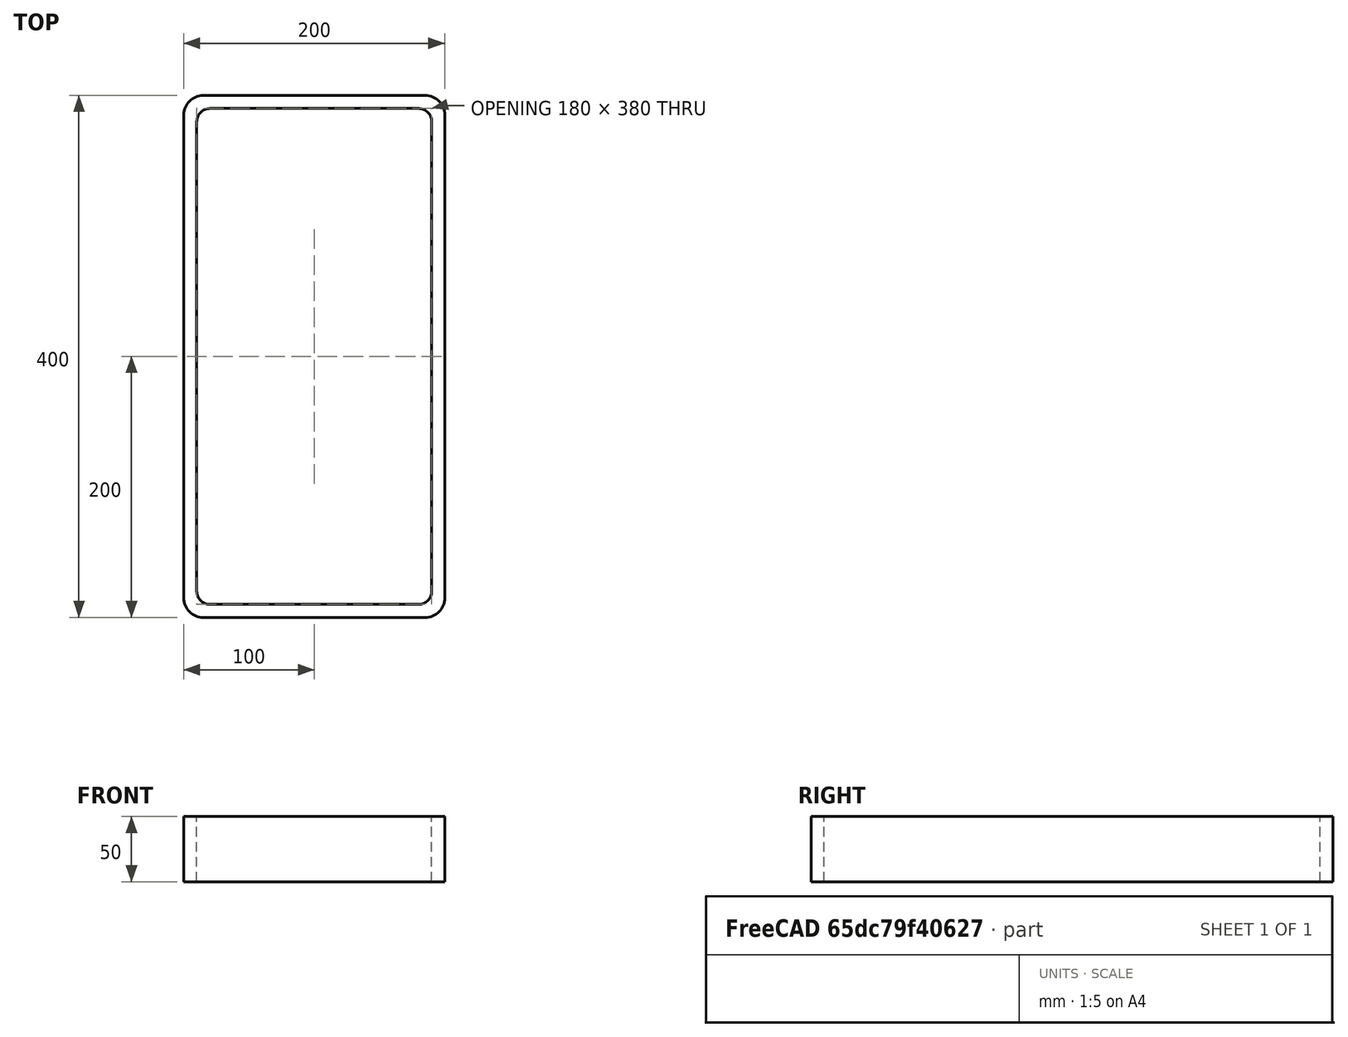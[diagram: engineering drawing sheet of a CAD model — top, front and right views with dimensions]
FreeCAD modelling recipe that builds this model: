
FCSTD DOCUMENT  (FreeCAD 0.15R4671 (Git))
Label: Rectangular hollow section 400x200x10 EN10219 S235JRH
License: All rights reserved
LicenseURL: http://en.wikipedia.org/wiki/All_rights_reserved
objects: Sketcher::SketchObject×1, Part::Extrusion×1
note: 2 computed .brp shape members not serialized (recipe doc carries the construction recipe); baked Part::Feature solids carry a one-line shape summary decoded from their .brp

FEATURE [Sketcher::SketchObject] Sketch
  sketch-geometry (16):
    g0: LineSegment StartX=-80 StartY=190 StartZ=0 EndX=80 EndY=190 EndZ=0
    g1: LineSegment StartX=90 StartY=180 StartZ=0 EndX=90 EndY=-180 EndZ=0
    g2: LineSegment StartX=80 StartY=-190 StartZ=0 EndX=-80 EndY=-190 EndZ=0
    g3: LineSegment StartX=-90 StartY=-180 StartZ=0 EndX=-90 EndY=180 EndZ=0
    g4: LineSegment StartX=-85 StartY=200 StartZ=0 EndX=85 EndY=200 EndZ=0
    g5: LineSegment StartX=100 StartY=185 StartZ=0 EndX=100 EndY=-185 EndZ=0
    g6: LineSegment StartX=85 StartY=-200 StartZ=0 EndX=-85 EndY=-200 EndZ=0
    g7: LineSegment StartX=-100 StartY=-185 StartZ=0 EndX=-100 EndY=185 EndZ=0
    g8: ArcOfCircle CenterX=-80 CenterY=180 CenterZ=0 NormalX=0 NormalY=0 NormalZ=1 Radius=10 StartAngle=1.5708 EndAngle=3.14159
    g9: ArcOfCircle CenterX=80 CenterY=180 CenterZ=0 NormalX=0 NormalY=0 NormalZ=1 Radius=10 StartAngle=0 EndAngle=1.5708
    g10: ArcOfCircle CenterX=80 CenterY=-180 CenterZ=0 NormalX=0 NormalY=0 NormalZ=1 Radius=10 StartAngle=4.71239 EndAngle=6.28319
    g11: ArcOfCircle CenterX=-80 CenterY=-180 CenterZ=0 NormalX=0 NormalY=0 NormalZ=1 Radius=10 StartAngle=3.14159 EndAngle=4.71239
    g12: ArcOfCircle CenterX=85 CenterY=185 CenterZ=0 NormalX=0 NormalY=0 NormalZ=1 Radius=15 StartAngle=0 EndAngle=1.5708
    g13: ArcOfCircle CenterX=85 CenterY=-185 CenterZ=0 NormalX=0 NormalY=0 NormalZ=1 Radius=15 StartAngle=4.71239 EndAngle=6.28319
    g14: ArcOfCircle CenterX=-85 CenterY=-185 CenterZ=0 NormalX=0 NormalY=0 NormalZ=1 Radius=15 StartAngle=3.14159 EndAngle=4.71239
    g15: ArcOfCircle CenterX=-85 CenterY=185 CenterZ=0 NormalX=0 NormalY=0 NormalZ=1 Radius=15 StartAngle=1.5708 EndAngle=3.14159
  constraints (36):
    c: Horizontal(g2)
    c: Vertical(g3)
    c: Horizontal(g6)
    c: Vertical(g7)
    c: Tangent(g3,g8) = 1.5708
    c: Tangent(g0,g8) = 1.5708
    c: Tangent(g0,g9) = 1.5708
    c: Tangent(g1,g9) = 1.5708
    c: Tangent(g1,g10) = 1.5708
    c: Tangent(g2,g10) = 1.5708
    c: Tangent(g2,g11) = 1.5708
    c: Tangent(g3,g11) = 1.5708
    c: Tangent(g4,g12) = 1.5708
    c: Tangent(g5,g12) = 1.5708
    c: Tangent(g5,g13) = 1.5708
    c: Tangent(g6,g13) = 1.5708
    c: Tangent(g6,g14) = 1.5708
    c: Tangent(g7,g14) = 1.5708
    c: Tangent(g7,g15) = 1.5708
    c: Tangent(g4,g15) = 1.5708
    c: Equal(g9,g8)
    c: Equal(g9,g11)
    c: Equal(g9,g10)
    c: Equal(g12,g15)
    c: Equal(g12,g14)
    c: Equal(g12,g13)
    c: Symmetric(g4,g6,g-1)
    c: Symmetric(g7,g5,g-2)
    c: DistanceY(g4,g6) = -400
    c: DistanceX(g7,g5) = 200
    c: Symmetric(g3,g1,g-2)
    c: Symmetric(g0,g2,g-1)
    c: DistanceY(g0,g4) = 10
    c: DistanceX(g5,g1) = -10
    c: Radius(g9) = 10
    c: Radius(g12) = 15
FEATURE [Part::Extrusion] Extrude  label="Rectangular hollow section 400x200x10 EN10219 S235JRH"
  Base = -> Sketch
  Dir = (0,0,50)
  Solid = true
